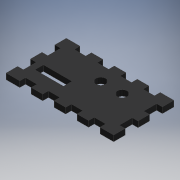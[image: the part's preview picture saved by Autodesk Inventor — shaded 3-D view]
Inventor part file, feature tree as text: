
AUTODESK INVENTOR PART (.ipt)
format: ipt  version: 2019 (Build 230136000, 136)  size: 189,440 bytes
history: native  units: mm
features: extrude x2, sketch x2
ambient origin geometry x8: Origin, YZ Plane, XZ Plane, XY Plane, X Axis, Y Axis, Z Axis, Center Point
bodies: Solid1 (feature_tree)
feature tree (4):
  extrude  "Extrusion1"  Depth=42.0mm
  extrude  "Extrusion2"  Depth=6.0mm
  sketch  "Sketch1"  dims[d0=75.0mm d1=42.0mm]
  sketch  "Sketch2"  dims[d2=20.0mm d3=6.0mm d4=12.0mm d5=8.0mm d6=7.0mm d7=28.0mm d8=38.0mm d9=15.0mm d10=4.0mm d11=0.0mm d12=4.0mm d13=4.0mm d14=8.0mm d15=8.0mm d16=8.0mm d17=8.0mm d18=4.0mm d19=4.0mm d20=0.0mm]
